# Revit family: Aspekt Casement Awning 3-1.25 Frame
name_source: partatom
category: Windows
units: mm (PartAtom-declared; Revit-internal decimal feet)

## family parameters
Always vertical = Yes
Cut with Voids When Loaded = Yes
Host = Wall
OmniClass Number = 23.30.20.00
OmniClass Title = Windows
Room Calculation Point = No
Shared = No

## types (1)
- Aspekt Casement Awning 3-1.25 Frame
    Analytic Construction = Double glazing - domestic SC=0.7
    Default Sill Height = 150 mm
    Heat Transfer Coefficient (U) = 2.8567 W/(m²·K)
    Height = 1000 mm  [stored 3.28084 ft]
    Manufacturer = REHAU
    Model = Aspekt Casement Awning 3-1.25 Frame
    REH_ACOUSTIC_ISOLATION = -
    REH_AIR_PERMEABILITY = -
    REH_DESCRIPTION = Material RAU-PVC, libre de plomo
Espesores de pared RAL-B o CEN B según UNE EN 12608
Sistema de estanqueidad Felpa con film seal
Profundidad constructiva 60 - 78 - 88 - 108  mm
Número de cámaras 2 (en hoja) - 3 (en marco)
Apoyo de la junta 8 mm
Coeficiente de transmisión térmica Uw 2,23 W/m2K
Insonorización Hasta Rw,P = 32 dB
Acabado superficial Folios imitación madera y colores según RAL
    REH_DESCRIPTION_LANGUAGE = LANGUAGE : ESPAÑOL
    REH_DESCRIPTION_LANGUAGE_ENG = LANGUAGE : ENGLISH
    REH_DESCRIPTION_LANGUAGE_SPA = LANGUAGE : ESPAÑOL
    REH_DESCRIPTION_SHORT = -
    REH_DESCRIPTION_SHORT_ENG = -
    REH_DESCRIPTION_SHORT_SPA = -
    REH_DISPLAY_ERROR_MESSAGE = Yes
    REH_ERROR_MESSAGE_VISIBLE (default) = No
    REH_GLAZING_CAPACITY = -
    REH_MAXIMUM_HEIGHT_EXCEEDED = 1300 mm
    REH_MAXIMUM_HEIGHT_EXCEEDED_1 = No
    REH_MAXIMUM_WEIGHT = 40.00 kg
    REH_MAXIMUM_WIDTH_EXCEEDED = 2000 mm
    REH_MAXIMUM_WIDTH_EXCEEDED_1 = No
    REH_Material = RAU-PVC
    REH_OPENING_TYPES = -
    REH_PROFILES_CONSTRUCTION_DEPTH = -
    REH_SECTIONS = -
    REH_SIZE_LIMIT_ERROR_OCCURRED = No
    REH_Unit Height = 1000 mm  [stored 3.28084 ft]
    REH_Unit Width = 1000 mm  [stored 3.28084 ft]
    REH_WATER_TIGHTNESS = -
    REH_WINDOWS_INSET = 150 mm
    REH_WIND_RESISTANCE = -
    Rough Height = 1000 mm  [stored 3.28084 ft]
    Rough Width = 1000 mm  [stored 3.28084 ft]
    Solar Heat Gain Coefficient = 0.7
    Thermal Resistance (R) = 0.3501 (m²·K)/W
    URL = www.rehau.com
    Uniclass 2015 Code = Ss_25_03
    Uniclass 2015 Name = Door and window systems
    Visual Light Transmittance = 0.78
    Wall Closure = By host
    Width = 1000 mm  [stored 3.28084 ft]
    ifcExportAs = ifcWindowsType
    ifcExportType = Door

note: [stored X ft] marks values corroborated as IEEE doubles in the binary element streams (Revit-internal decimal feet)

## geometry (parser evidence)
native form markers: Sweep x5
no freeform markers — native parametric forms only
